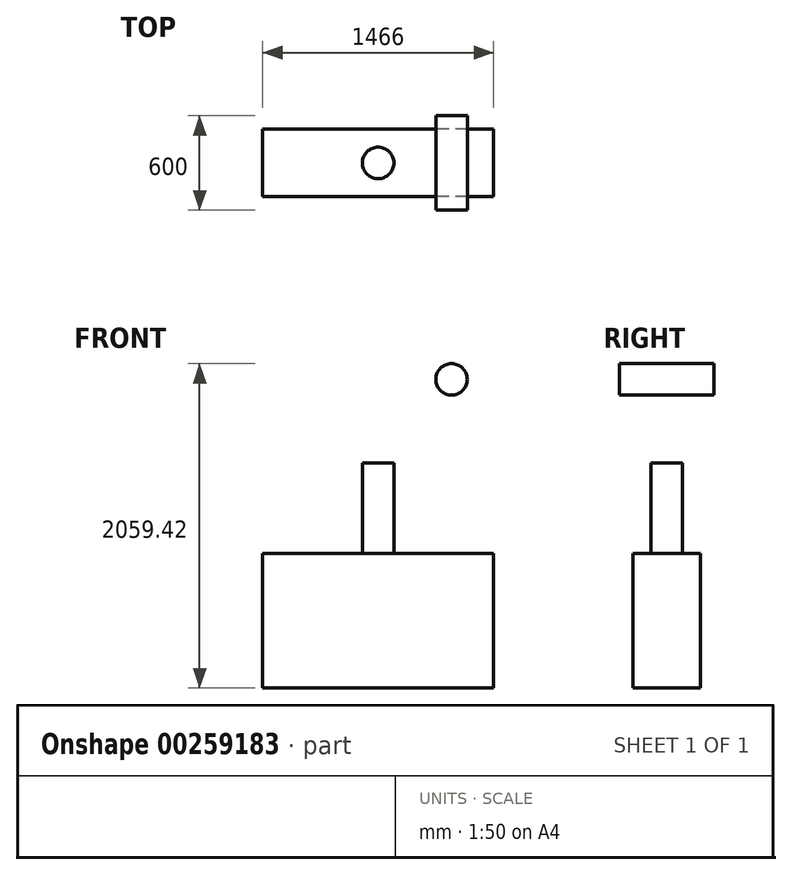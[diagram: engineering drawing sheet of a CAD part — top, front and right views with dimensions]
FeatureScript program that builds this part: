
annotation { "Feature Type Name" : "Feature", "Feature Type Description" : "" }
export const myFeature = defineFeature(function(context is Context, id is Id, definition is map)
    precondition{}
    {
        {
            var Q0;
            Q0=qCreatedBy(makeId("Front.planeOp"),FACE);
            var sketch = newSketch(context, id + "F0", { "sketchPlane" : qUnion([Q0])});
            skLineSegment(sketch, "E0.bottom", {"start": v(733, -427.2) * mm, "end": v(-733, -427.2) * mm});
            skLineSegment(sketch, "E0.top", {"start": v(733, 427.2) * mm, "end": v(-733, 427.2) * mm});
            skLineSegment(sketch, "E0.left", {"start": v(733, -427.2) * mm, "end": v(733, 427.2) * mm});
            skLineSegment(sketch, "E0.right", {"start": v(-733, -427.2) * mm, "end": v(-733, 427.2) * mm});
            skPoint(sketch, "E0.middle", {"position": v(0, 0) * mm});
            skCircle(sketch, "E1", {"center": v(466.38, 1532.2) * mm, "radius": 100 * mm});
            skSolve(sketch);
        }
        {
            var Q0;
            Q0=makeQuery(id+"F0.imprint","IMPRINT",FACE,{"disambiguationData":[TD([[makeQuery(id+"F0.imprint","IMPRINT",EDGE,{"derivedFrom":sQuery(id+"F0.wireOp",EDGE,"E0.bottom")}),-1.0]])]});
            extrude(context, id + "F1", {"entities" : qUnion([Q0]), "endBound" : BoundingType.SYMMETRIC, "depth" : 430 * mm});
        }
        {
            var Q0;
            Q0=makeQuery(id+"F0.imprint","IMPRINT",FACE,{"disambiguationData":[TD([[makeQuery(id+"F0.imprint","IMPRINT",EDGE,{"derivedFrom":sQuery(id+"F0.wireOp",EDGE,"E1")}),1.0]])]});
            extrude(context, id + "F2", {"entities" : qUnion([Q0]), "endBound" : BoundingType.SYMMETRIC, "depth" : 600 * mm});
        }
        {
            var Q0;
            Q0=qCreatedBy(makeId("Top.planeOp"),FACE);
            var sketch = newSketch(context, id + "F3", { "sketchPlane" : qUnion([Q0])});
            skCircle(sketch, "E2", {"center": v(0, 0) * mm, "radius": 100 * mm});
            skSolve(sketch);
        }
        {
            var Q0;
            Q0 = qSketchRegion(id + "F3", true);
            extrude(context, id + "F4", {"entities" : qUnion([Q0]), "operationType" : NewBodyOperationType.ADD, "depth" : 1000 * mm});
        }
    });
